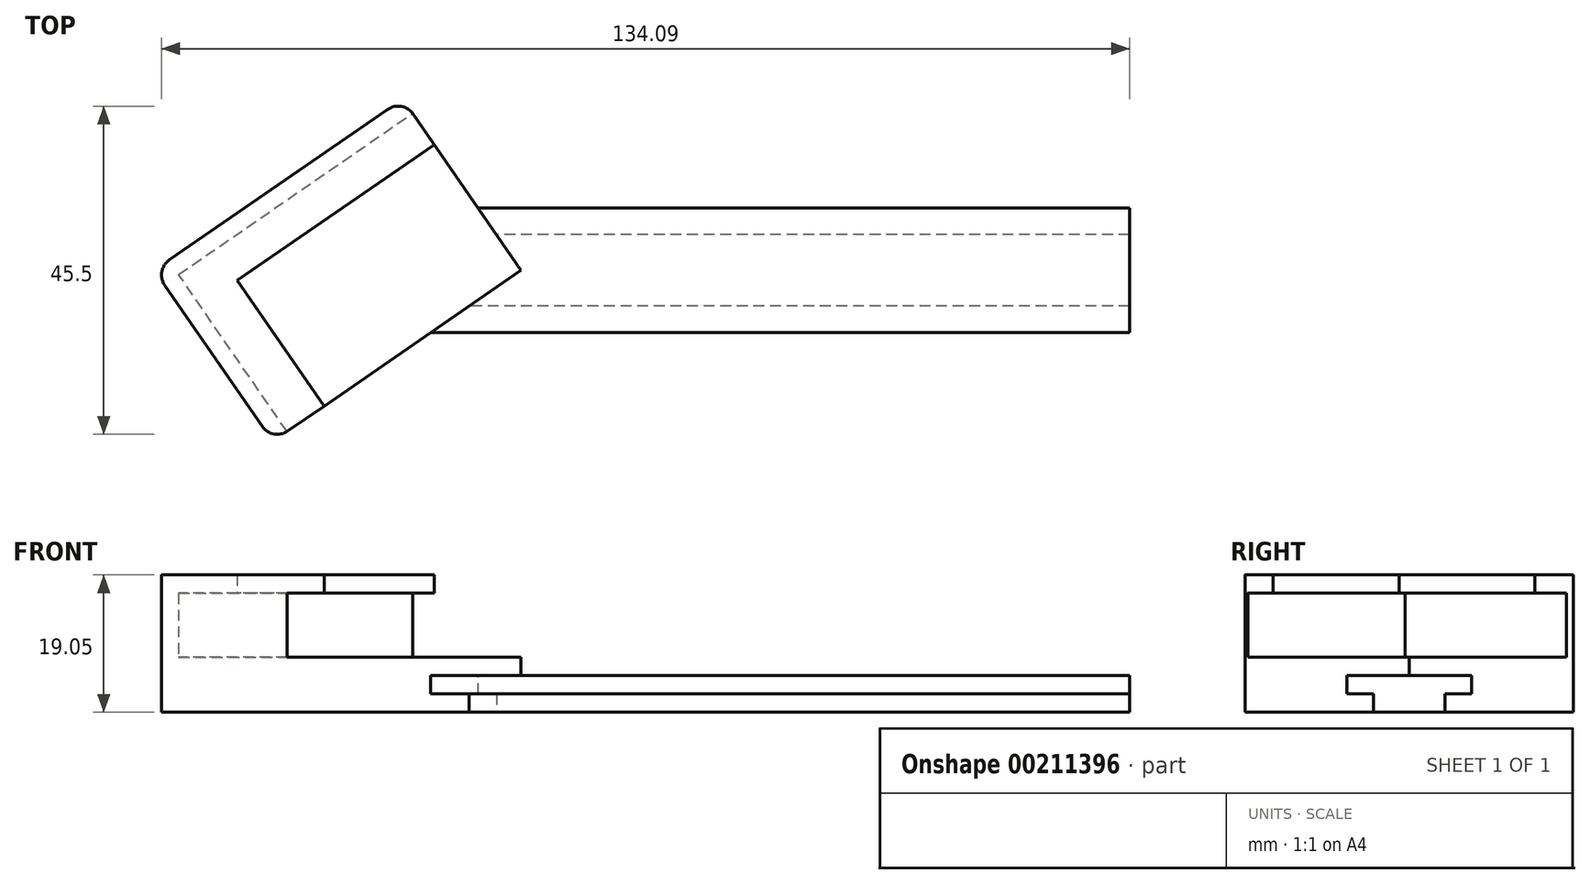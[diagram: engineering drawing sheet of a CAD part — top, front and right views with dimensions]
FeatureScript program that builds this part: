
annotation { "Feature Type Name" : "Feature", "Feature Type Description" : "" }
export const myFeature = defineFeature(function(context is Context, id is Id, definition is map)
    precondition{}
    {
        {
            var Q0;
            Q0=qCreatedBy(makeId("Right.planeOp"),FACE);
            var sketch = newSketch(context, id + "F0", { "sketchPlane" : qUnion([Q0])});
            skLineSegment(sketch, "E0.bottom", {"start": v(12.7, -3.81) * mm, "end": v(-12.7, -3.81) * mm, "construction": true});
            skLineSegment(sketch, "E0.top", {"start": v(12.7, 3.8) * mm, "end": v(-12.7, 3.8) * mm, "construction": true});
            skLineSegment(sketch, "E0.left", {"start": v(12.7, -3.8) * mm, "end": v(12.7, 3.81) * mm, "construction": true});
            skLineSegment(sketch, "E0.right", {"start": v(-12.7, -3.8) * mm, "end": v(-12.7, 3.81) * mm, "construction": true});
            skPoint(sketch, "E0.middle", {"position": v(0, 0) * mm});
            skLineSegment(sketch, "E1", {"start": v(-8.64, 1.27) * mm, "end": v(8.64, 1.27) * mm});
            skLineSegment(sketch, "E2", {"start": v(8.64, 1.27) * mm, "end": v(8.64, -1.27) * mm});
            skLineSegment(sketch, "E3", {"start": v(8.64, -1.27) * mm, "end": v(4.95, -1.27) * mm});
            skLineSegment(sketch, "E4", {"start": v(4.95, -1.27) * mm, "end": v(4.95, -3.8) * mm});
            skLineSegment(sketch, "E5", {"start": v(4.95, -3.81) * mm, "end": v(-4.95, -3.81) * mm});
            skLineSegment(sketch, "E6", {"start": v(-4.95, -3.8) * mm, "end": v(-4.95, -1.27) * mm});
            skLineSegment(sketch, "E7", {"start": v(-4.95, -1.27) * mm, "end": v(-8.64, -1.27) * mm});
            skLineSegment(sketch, "E8", {"start": v(-8.64, -1.27) * mm, "end": v(-8.64, 1.27) * mm});
            skLineSegment(sketch, "E9", {"start": v(-12.7, 3.81) * mm, "end": v(-8.64, 1.27) * mm, "construction": true});
            skLineSegment(sketch, "E10", {"start": v(8.64, 1.27) * mm, "end": v(12.7, 3.8) * mm, "construction": true});
            skLineSegment(sketch, "E11", {"start": v(8.64, -1.27) * mm, "end": v(12.7, -3.8) * mm, "construction": true});
            skLineSegment(sketch, "E12", {"start": v(-8.64, -1.27) * mm, "end": v(-12.7, -3.81) * mm, "construction": true});
            skLineSegment(sketch, "E13", {"start": v(-4.95, -1.27) * mm, "end": v(4.95, -1.27) * mm, "construction": true});
            skSolve(sketch);
        }
        {
            var Q0;
            Q0 = qSketchRegion(id + "F0", true);
            extrude(context, id + "F1", {"entities" : qUnion([Q0]), "endBound" : BoundingType.SYMMETRIC, "depth" : 102.36 * mm});
        }
        {
            var Q0;
            Q0=qCreatedBy(makeId("Top.planeOp"),FACE);
            var sketch = newSketch(context, id + "F2", { "sketchPlane" : qUnion([Q0])});
            skLineSegment(sketch, "E14", {"start": v(-33.1, 0) * mm, "end": v(-48.05, 21.66) * mm});
            skLineSegment(sketch, "E15", {"start": v(-51.59, 22.3) * mm, "end": v(-81.82, 1.44) * mm});
            skLineSegment(sketch, "E16", {"start": v(-82.46, -2.1) * mm, "end": v(-68.96, -21.66) * mm});
            skLineSegment(sketch, "E17", {"start": v(-65.43, -22.3) * mm, "end": v(-33.1, 0) * mm});
            skPoint(sketch, "E18.visualSharp", {"position": v(-83.9, 0) * mm});
            skArc(sketch, "E18.filletArc", {"start": v(-81.82, 1.44) * mm, "mid": v(-82.87, -0.19) * mm, "end": v(-82.46, -2.1) * mm});
            skPoint(sketch, "E19.visualSharp", {"position": v(-49.5, 23.75) * mm});
            skArc(sketch, "E19.filletArc", {"start": v(-48.05, 21.66) * mm, "mid": v(-49.69, 22.71) * mm, "end": v(-51.59, 22.3) * mm});
            skPoint(sketch, "E20.visualSharp", {"position": v(-67.52, -23.75) * mm});
            skArc(sketch, "E20.filletArc", {"start": v(-68.96, -21.66) * mm, "mid": v(-67.33, -22.71) * mm, "end": v(-65.43, -22.3) * mm});
            skLineSegment(sketch, "E21", {"start": v(-83.9, 0) * mm, "end": v(0, 0) * mm, "construction": true});
            skSolve(sketch);
        }
        {
            var Q0;
            Q0 = qSketchRegion(id + "F2", true);
            extrude(context, id + "F3", {"entities" : qUnion([Q0]), "operationType" : NewBodyOperationType.ADD, "depth" : 15.24 * mm});
        }
        {
            var Q0;
            Q0 = qSketchRegion(id + "F2", true);
            extrude(context, id + "F4", {"entities" : qUnion([Q0]), "operationType" : NewBodyOperationType.ADD, "oppositeDirection" : true, "depth" : 3.8 * mm});
        }
        {
            var Q0;
            Q0=makeQuery(id+"F1.opExtrude","SWEPT_FACE",FACE,{"disambiguationData":[OSD([sQuery(id+"F0.wireOp",EDGE,"E1")])]});
            var sketch = newSketch(context, id + "F5", { "sketchPlane" : qUnion([Q0])});
            skLineSegment(sketch, "E22", {"start": v(-80.55, -0.6) * mm, "end": v(-40.43, 27.08) * mm});
            skLineSegment(sketch, "E23", {"start": v(-40.43, 27.08) * mm, "end": v(-21.74, 0) * mm});
            skLineSegment(sketch, "E24", {"start": v(-21.74, 0) * mm, "end": v(-61.86, -27.68) * mm});
            skLineSegment(sketch, "E25", {"start": v(-61.86, -27.68) * mm, "end": v(-80.55, -0.6) * mm});
            skSolve(sketch);
        }
        {
            var Q0;
            Q0 = qSketchRegion(id + "F5", true);
            extrude(context, id + "F6", {"entities" : qUnion([Q0]), "operationType" : NewBodyOperationType.REMOVE, "depth" : 11.43 * mm, "hasSecondDirection" : true, "secondDirectionOppositeDirection" : false, "secondDirectionDepth" : 2.54 * mm});
        }
        {
            var Q0;
            Q0=makeQuery(id+"F6.boolean.opBoolean","MERGE",FACE,{"derivedFrom":[makeQuery(id+"F1.opExtrude","SWEPT_FACE",FACE,{"disambiguationData":[OSD([sQuery(id+"F0.wireOp",EDGE,"E1")])]}),makeQuery(id+"F6.opExtrude","CAP_FACE",FACE,{"disambiguationData":[OSD([sQuery(id+"F5.wireOp",EDGE,"E22"),sQuery(id+"F5.wireOp",EDGE,"E23"),sQuery(id+"F5.wireOp",EDGE,"E24"),sQuery(id+"F5.wireOp",EDGE,"E25")])],"isStart":true})]});
            var sketch = newSketch(context, id + "F7", { "sketchPlane" : qUnion([Q0])});
            skLineSegment(sketch, "E26", {"start": v(-72.43, -1.41) * mm, "end": v(-40.43, 20.67) * mm});
            skLineSegment(sketch, "E27", {"start": v(-40.43, 20.67) * mm, "end": v(-25.75, -0.6) * mm});
            skLineSegment(sketch, "E28", {"start": v(-25.75, -0.6) * mm, "end": v(-57.75, -22.68) * mm});
            skLineSegment(sketch, "E29", {"start": v(-57.75, -22.68) * mm, "end": v(-72.43, -1.41) * mm});
            skSolve(sketch);
        }
        {
            var Q0;
            Q0 = qSketchRegion(id + "F7", true);
            var Q1;
            Q1=makeQuery(id+"F6.boolean.opBoolean","COPY",FACE,{"derivedFrom":makeQuery(id+"F6.opExtrude","CAP_FACE",FACE,{"disambiguationData":[OSD([sQuery(id+"F5.wireOp",EDGE,"E22"),sQuery(id+"F5.wireOp",EDGE,"E23"),sQuery(id+"F5.wireOp",EDGE,"E24"),sQuery(id+"F5.wireOp",EDGE,"E25")])],"isStart":true})});
            extrude(context, id + "F8", {"entities" : qUnion([Q0]), "operationType" : NewBodyOperationType.REMOVE, "depth" : 23.1 * mm, "hasSecondDirection" : true, "secondDirectionBound" : SecondDirectionBoundingType.UP_TO_SURFACE, "secondDirectionOppositeDirection" : false, "secondDirectionBoundEntityFace" : qUnion([Q1]), "secondDirectionDepth" : 2.95 * mm});
        }
    });
